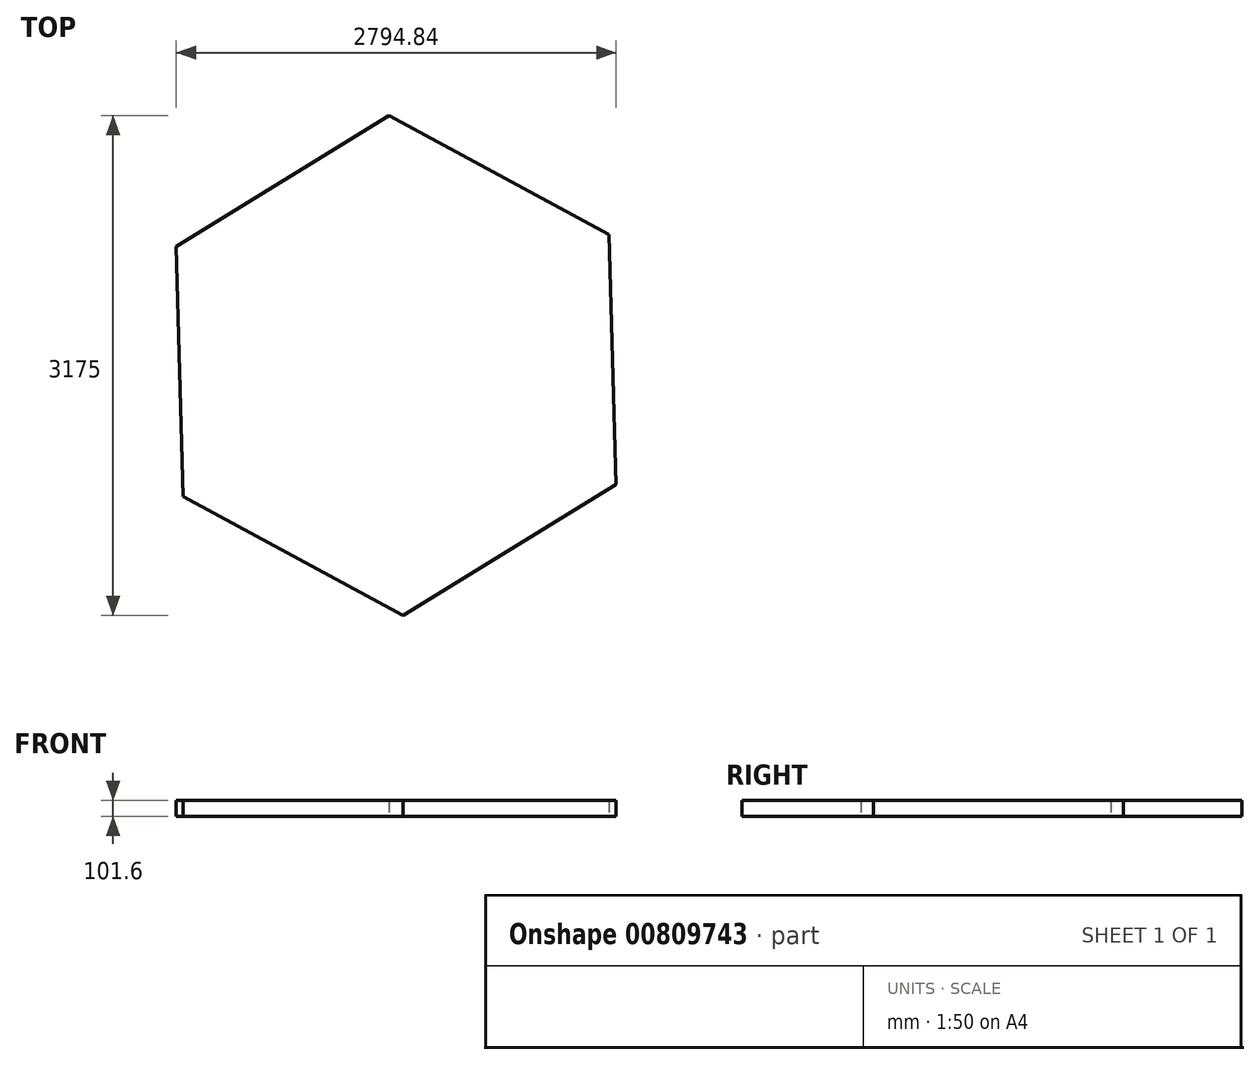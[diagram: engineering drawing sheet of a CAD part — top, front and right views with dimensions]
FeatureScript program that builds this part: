
annotation { "Feature Type Name" : "Feature", "Feature Type Description" : "" }
export const myFeature = defineFeature(function(context is Context, id is Id, definition is map)
    precondition{}
    {
        {
            var Q0;
            Q0=qCreatedBy(makeId("Top.planeOp"),FACE);
            var sketch = newSketch(context, id + "F0", { "sketchPlane" : qUnion([Q0])});
            skCircle(sketch, "E0.cCircle", {"center": v(0, 0) * mm, "radius": 1375.37 * mm, "construction": true});
            skLineSegment(sketch, "E0.0", {"start": v(1397.42, -754.6) * mm, "end": v(45.22, -1587.5) * mm});
            skLineSegment(sketch, "E0.1", {"start": v(45.22, -1587.5) * mm, "end": v(-1352.2, -832.9) * mm});
            skLineSegment(sketch, "E0.2", {"start": v(-1352.2, -832.9) * mm, "end": v(-1397.42, 754.6) * mm});
            skLineSegment(sketch, "E0.3", {"start": v(-1397.42, 754.6) * mm, "end": v(-45.22, 1587.5) * mm});
            skLineSegment(sketch, "E0.4", {"start": v(-45.22, 1587.5) * mm, "end": v(1352.2, 832.9) * mm});
            skLineSegment(sketch, "E0.5", {"start": v(1352.2, 832.9) * mm, "end": v(1397.42, -754.6) * mm});
            skPoint(sketch, "E0.0.midPoint", {"position": v(721.32, -1171.05) * mm});
            skSolve(sketch);
        }
        {
            var Q0;
            Q0 = qSketchRegion(id + "F0", true);
            extrude(context, id + "F1", {"entities" : qUnion([Q0]), "depth" : 101.6 * mm, "offsetDistance" : 25.4 * mm});
        }
    });
